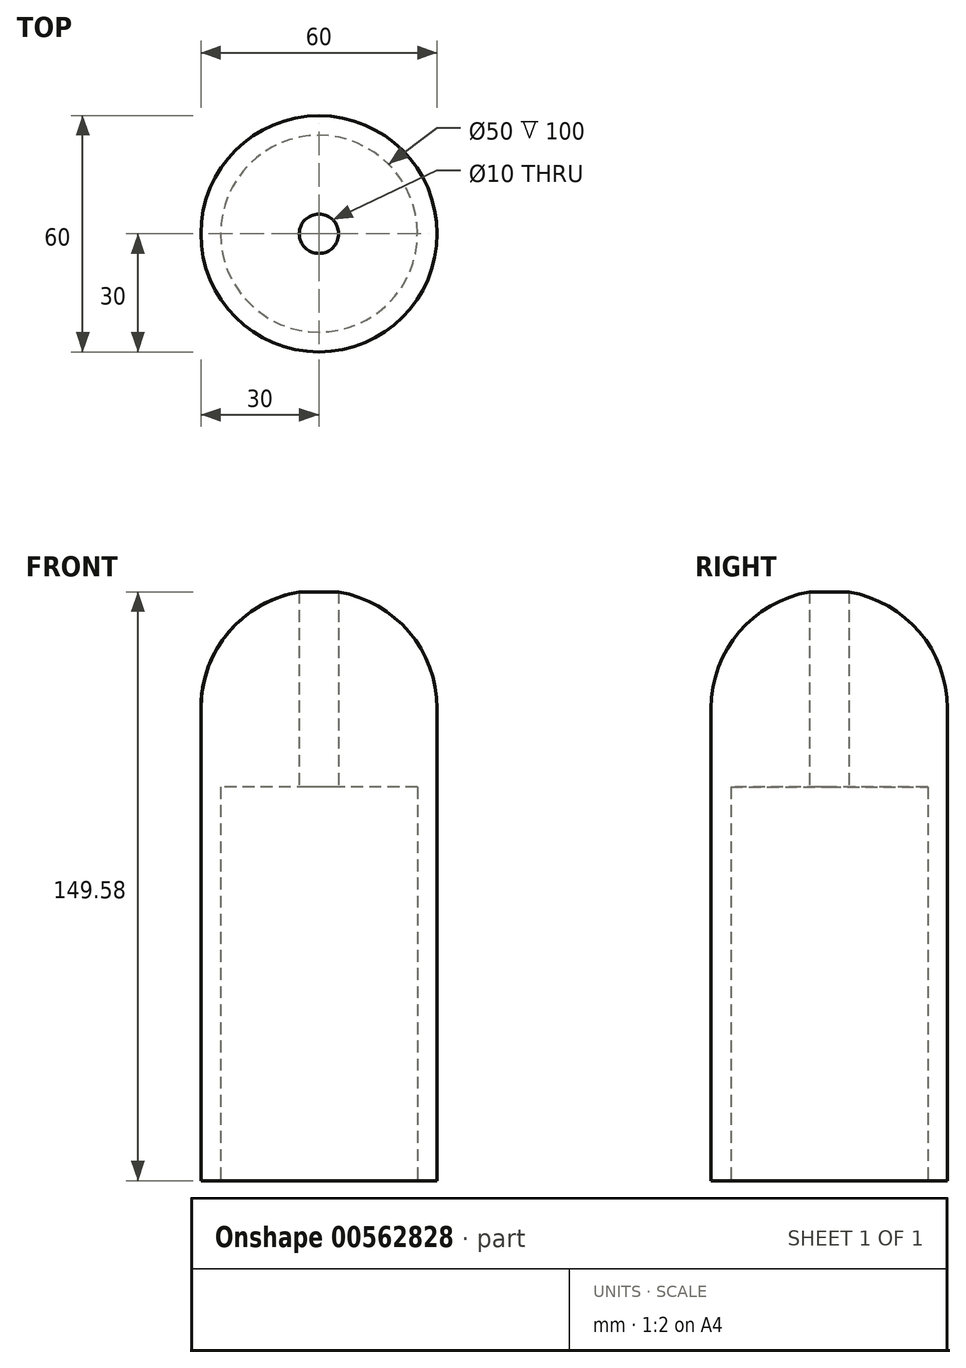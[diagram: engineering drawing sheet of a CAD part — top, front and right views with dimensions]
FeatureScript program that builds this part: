
annotation { "Feature Type Name" : "Feature", "Feature Type Description" : "" }
export const myFeature = defineFeature(function(context is Context, id is Id, definition is map)
    precondition{}
    {
        {
            var Q0;
            Q0=qCreatedBy(makeId("Front.planeOp"),FACE);
            var sketch = newSketch(context, id + "F0", { "sketchPlane" : qUnion([Q0])});
            skLineSegment(sketch, "E0.bottom", {"start": v(0, 0) * mm, "end": v(-30, 0) * mm});
            skLineSegment(sketch, "E0.top", {"start": v(0, 150) * mm, "end": v(0, 150) * mm});
            skLineSegment(sketch, "E0.left", {"start": v(0, 0) * mm, "end": v(0, 150) * mm});
            skLineSegment(sketch, "E0.right", {"start": v(-30, 0) * mm, "end": v(-30, 120) * mm});
            skPoint(sketch, "E1.visualSharp", {"position": v(-30, 150) * mm});
            skArc(sketch, "E1.filletArc", {"start": v(0, 150) * mm, "mid": v(-21.21, 141.21) * mm, "end": v(-30, 120) * mm});
            skSolve(sketch);
        }
        {
            var Q0;
            Q0 = qSketchRegion(id + "F0", true);
            var Q1;
            Q1=sQuery(id+"F0.wireOp",EDGE,"E0.left");
            revolve(context, id + "F1", {"entities" : qUnion([Q0]), "axis" : qUnion([Q1]), "revolveType" : RevolveType.FULL});
        }
        {
            var Q0;
            Q0=qCreatedBy(makeId("Top.planeOp"),FACE);
            var sketch = newSketch(context, id + "F2", { "sketchPlane" : qUnion([Q0])});
            skCircle(sketch, "E2", {"center": v(0, 0) * mm, "radius": 25 * mm});
            skSolve(sketch);
        }
        {
            var Q0;
            Q0 = qSketchRegion(id + "F2", true);
            extrude(context, id + "F3", {"entities" : qUnion([Q0]), "operationType" : NewBodyOperationType.REMOVE, "depth" : 100 * mm, "offsetDistance" : 25 * mm});
        }
        {
            var Q0;
            Q0=qCreatedBy(makeId("Top.planeOp"),FACE);
            var sketch = newSketch(context, id + "F4", { "sketchPlane" : qUnion([Q0])});
            skCircle(sketch, "E3", {"center": v(0, 0) * mm, "radius": 5 * mm});
            skSolve(sketch);
        }
        {
            var Q0;
            Q0 = qSketchRegion(id + "F4", true);
            extrude(context, id + "F5", {"entities" : qUnion([Q0]), "operationType" : NewBodyOperationType.REMOVE, "endBound" : BoundingType.THROUGH_ALL, "depth" : 25 * mm, "offsetDistance" : 25 * mm});
        }
    });
